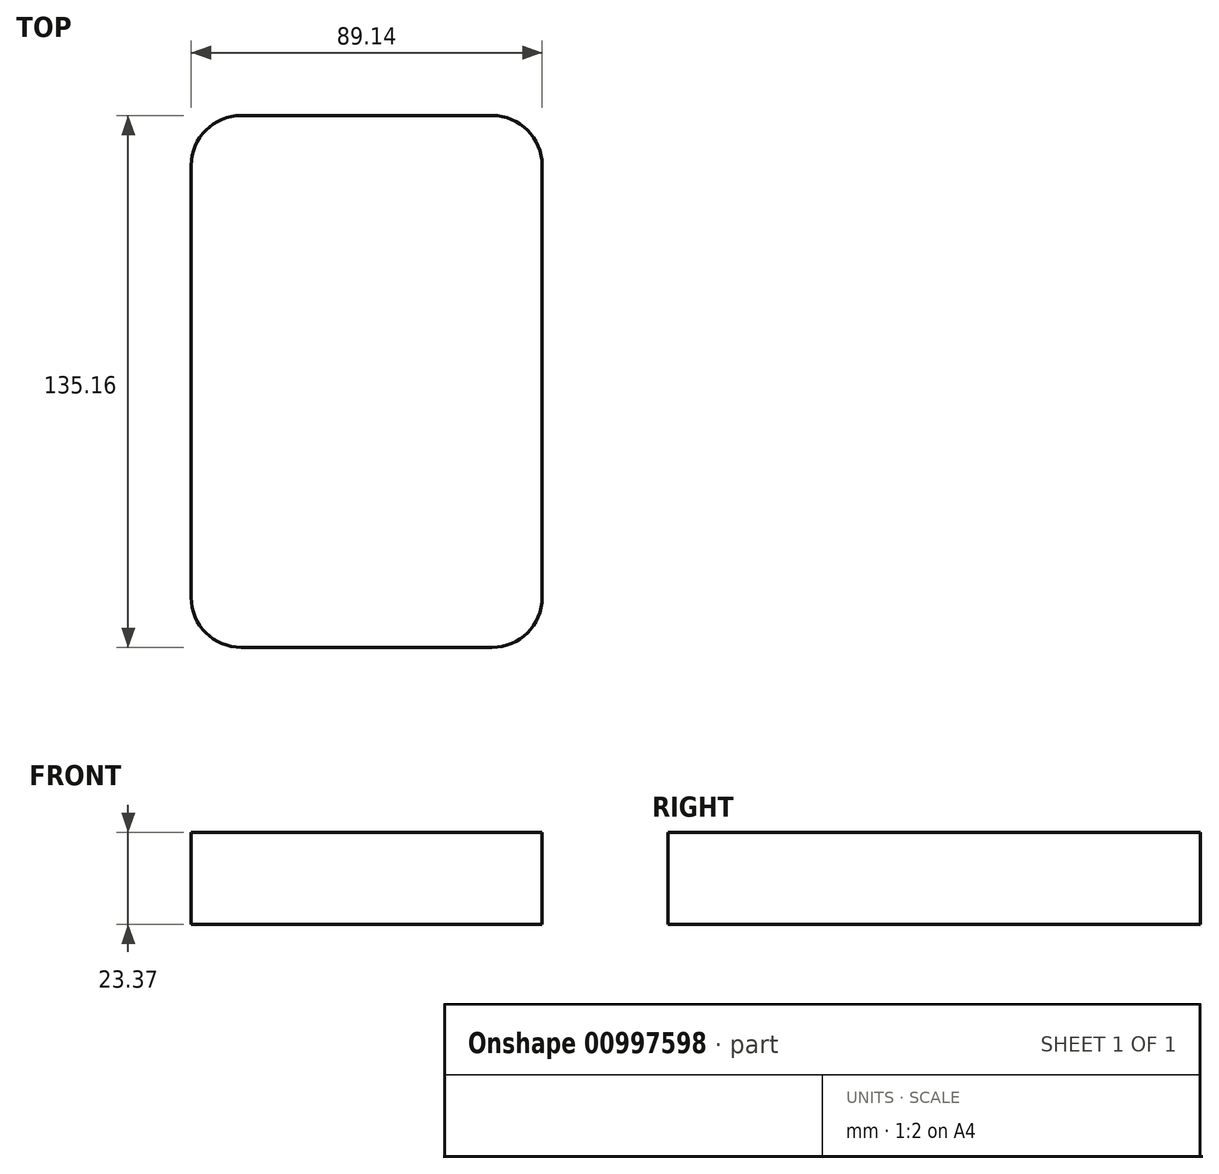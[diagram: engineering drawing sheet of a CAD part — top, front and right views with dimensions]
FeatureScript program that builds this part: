
annotation { "Feature Type Name" : "Feature", "Feature Type Description" : "" }
export const myFeature = defineFeature(function(context is Context, id is Id, definition is map)
    precondition{}
    {
        {
            var Q0;
            Q0=qCreatedBy(makeId("Top.planeOp"),FACE);
            var sketch = newSketch(context, id + "F0", { "sketchPlane" : qUnion([Q0])});
            skLineSegment(sketch, "E0.bottom", {"start": v(31.87, 67.58) * mm, "end": v(-31.87, 67.58) * mm});
            skLineSegment(sketch, "E0.top", {"start": v(31.87, -67.58) * mm, "end": v(-31.87, -67.58) * mm});
            skLineSegment(sketch, "E0.left", {"start": v(44.57, 54.88) * mm, "end": v(44.57, -54.88) * mm});
            skLineSegment(sketch, "E0.right", {"start": v(-44.57, 54.88) * mm, "end": v(-44.57, -54.88) * mm});
            skPoint(sketch, "E0.middle", {"position": v(0, 0) * mm});
            skPoint(sketch, "E1.visualSharp", {"position": v(-44.57, -67.58) * mm});
            skArc(sketch, "E1.filletArc", {"start": v(-44.57, -54.88) * mm, "mid": v(-40.85, -63.86) * mm, "end": v(-31.87, -67.58) * mm});
            skPoint(sketch, "E2.visualSharp", {"position": v(-44.57, 67.58) * mm});
            skArc(sketch, "E2.filletArc", {"start": v(-31.87, 67.58) * mm, "mid": v(-40.85, 63.86) * mm, "end": v(-44.57, 54.88) * mm});
            skPoint(sketch, "E3.visualSharp", {"position": v(44.57, 67.58) * mm});
            skArc(sketch, "E3.filletArc", {"start": v(44.57, 54.88) * mm, "mid": v(40.85, 63.86) * mm, "end": v(31.87, 67.58) * mm});
            skPoint(sketch, "E4.visualSharp", {"position": v(44.57, -67.58) * mm});
            skArc(sketch, "E4.filletArc", {"start": v(31.87, -67.58) * mm, "mid": v(40.85, -63.86) * mm, "end": v(44.57, -54.88) * mm});
            skSolve(sketch);
        }
        {
            var Q0;
            Q0=makeQuery(id+"F0.imprint","IMPRINT",FACE,{"disambiguationData":[TD([[makeQuery(id+"F0.imprint","IMPRINT",EDGE,{"derivedFrom":sQuery(id+"F0.wireOp",EDGE,"E0.bottom")}),1.0]])]});
            extrude(context, id + "F1", {"entities" : qUnion([Q0]), "depth" : 23.37 * mm, "offsetDistance" : 25.4 * mm});
        }
    });
